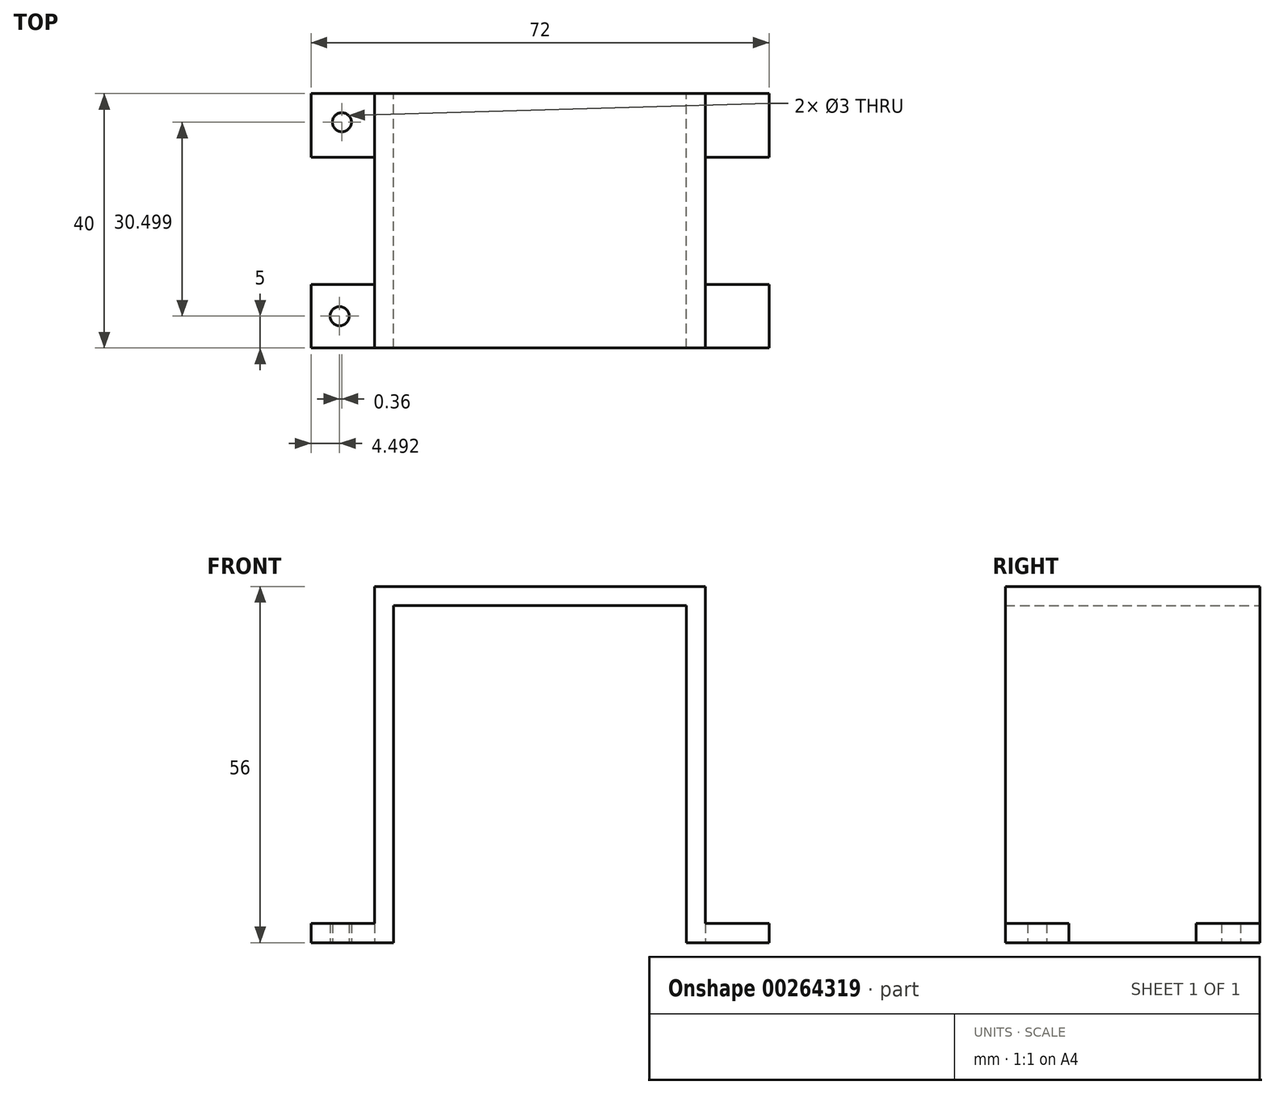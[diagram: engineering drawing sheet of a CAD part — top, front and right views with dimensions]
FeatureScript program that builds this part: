
annotation { "Feature Type Name" : "Feature", "Feature Type Description" : "" }
export const myFeature = defineFeature(function(context is Context, id is Id, definition is map)
    precondition{}
    {
        {
            var Q0;
            Q0=qCreatedBy(makeId("Front.planeOp"),FACE);
            var sketch = newSketch(context, id + "F0", { "sketchPlane" : qUnion([Q0])});
            skLineSegment(sketch, "E0", {"start": v(-56.16, -56) * mm, "end": v(-56.16, 0) * mm});
            skLineSegment(sketch, "E1", {"start": v(-56.16, 0) * mm, "end": v(-4.16, 0) * mm});
            skLineSegment(sketch, "E2", {"start": v(-4.16, 0) * mm, "end": v(-4.16, -56) * mm});
            skLineSegment(sketch, "E3", {"start": v(-4.16, -56) * mm, "end": v(-7.16, -56) * mm});
            skLineSegment(sketch, "E4", {"start": v(-7.16, -56) * mm, "end": v(-7.16, -3) * mm});
            skLineSegment(sketch, "E5", {"start": v(-7.16, -3) * mm, "end": v(-53.16, -3) * mm});
            skLineSegment(sketch, "E6", {"start": v(-56.16, -56) * mm, "end": v(-53.16, -56) * mm});
            skLineSegment(sketch, "E7", {"start": v(-53.16, -56) * mm, "end": v(-53.16, -3) * mm});
            skSolve(sketch);
        }
        {
            var Q0;
            Q0=makeQuery(id+"F0.imprint","IMPRINT",FACE,{"disambiguationData":[TD([[makeQuery(id+"F0.imprint","IMPRINT",EDGE,{"derivedFrom":sQuery(id+"F0.wireOp",EDGE,"trVvDC30-jFMu-2vVs-1iuF-PGvGUxvKBNX2.bottom")}),-1.0]])]});
            var Q1;
            Q1=makeQuery(id+"F0.imprint","IMPRINT",FACE,{"disambiguationData":[TD([[makeQuery(id+"F0.imprint","IMPRINT",EDGE,{"derivedFrom":sQuery(id+"F0.wireOp",EDGE,"E0")}),-1.0]])]});
            extrude(context, id + "F1", {"entities" : qUnion([Q0, Q1]), "depth" : 40 * mm});
        }
        {
            var Q0;
            Q0=makeQuery(id+"F1.opExtrude","SWEPT_FACE",FACE,{"disambiguationData":[OSD([sQuery(id+"F0.wireOp",EDGE,"E6")])]});
            var sketch = newSketch(context, id + "F2", { "sketchPlane" : qUnion([Q0])});
            skLineSegment(sketch, "E8.bottom", {"start": v(-56.16, 0) * mm, "end": v(-66.16, 0) * mm});
            skLineSegment(sketch, "E8.top", {"start": v(-56.16, 10) * mm, "end": v(-66.16, 10) * mm});
            skLineSegment(sketch, "E8.left", {"start": v(-56.16, 0) * mm, "end": v(-56.16, 10) * mm});
            skLineSegment(sketch, "E8.right", {"start": v(-66.16, 0) * mm, "end": v(-66.16, 10) * mm});
            skLineSegment(sketch, "E9.bottom", {"start": v(-56.16, 40) * mm, "end": v(-66.16, 40) * mm});
            skLineSegment(sketch, "E9.top", {"start": v(-56.16, 30) * mm, "end": v(-66.16, 30) * mm});
            skLineSegment(sketch, "E9.left", {"start": v(-56.16, 40) * mm, "end": v(-56.16, 30) * mm});
            skLineSegment(sketch, "E9.right", {"start": v(-66.16, 40) * mm, "end": v(-66.16, 30) * mm});
            skSolve(sketch);
        }
        {
            var Q0;
            Q0=makeQuery(id+"F1.opExtrude","SWEPT_FACE",FACE,{"disambiguationData":[OSD([sQuery(id+"F0.wireOp",EDGE,"E3")])]});
            var sketch = newSketch(context, id + "F3", { "sketchPlane" : qUnion([Q0])});
            skLineSegment(sketch, "E10.bottom", {"start": v(-4.16, 40) * mm, "end": v(5.84, 40) * mm});
            skLineSegment(sketch, "E10.top", {"start": v(-4.16, 30) * mm, "end": v(5.84, 30) * mm});
            skLineSegment(sketch, "E10.left", {"start": v(-4.16, 40) * mm, "end": v(-4.16, 30) * mm});
            skLineSegment(sketch, "E10.right", {"start": v(5.84, 40) * mm, "end": v(5.84, 30) * mm});
            skLineSegment(sketch, "E11.bottom", {"start": v(-4.16, 0) * mm, "end": v(5.84, 0) * mm});
            skLineSegment(sketch, "E11.top", {"start": v(-4.16, 10) * mm, "end": v(5.84, 10) * mm});
            skLineSegment(sketch, "E11.left", {"start": v(-4.16, 0) * mm, "end": v(-4.16, 10) * mm});
            skLineSegment(sketch, "E11.right", {"start": v(5.84, 0) * mm, "end": v(5.84, 10) * mm});
            skCircle(sketch, "E12", {"center": v(19.06, 35.17) * mm, "radius": 1.67 * mm});
            skSolve(sketch);
        }
        {
            var Q0;
            Q0=makeQuery(id+"F3.imprint","IMPRINT",FACE,{"disambiguationData":[TD([[makeQuery(id+"F3.imprint","IMPRINT",EDGE,{"derivedFrom":sQuery(id+"F3.wireOp",EDGE,"E11.bottom")}),1.0]])]});
            extrude(context, id + "F4", {"entities" : qUnion([Q0]), "operationType" : NewBodyOperationType.ADD, "oppositeDirection" : true, "depth" : 3 * mm});
        }
        {
            var Q0;
            Q0=makeQuery(id+"F2.imprint","IMPRINT",FACE,{"disambiguationData":[TD([[makeQuery(id+"F2.imprint","IMPRINT",EDGE,{"derivedFrom":sQuery(id+"F2.wireOp",EDGE,"E8.bottom")}),-1.0]])]});
            extrude(context, id + "F5", {"entities" : qUnion([Q0]), "operationType" : NewBodyOperationType.ADD, "oppositeDirection" : true, "depth" : 3 * mm});
        }
        {
            var Q0;
            Q0=makeQuery(id+"F4.boolean.opBoolean","MERGE",FACE,{"derivedFrom":[makeQuery(id+"F1.opExtrude","SWEPT_FACE",FACE,{"disambiguationData":[OSD([sQuery(id+"F0.wireOp",EDGE,"E3")])]}),makeQuery(id+"F4.opExtrude","CAP_FACE",FACE,{"disambiguationData":[OSD([sQuery(id+"F3.wireOp",EDGE,"E11.bottom"),sQuery(id+"F3.wireOp",EDGE,"E11.top"),sQuery(id+"F3.wireOp",EDGE,"E11.left"),sQuery(id+"F3.wireOp",EDGE,"E11.right")])],"isStart":true})]});
            var sketch = newSketch(context, id + "F6", { "sketchPlane" : qUnion([Q0])});
            skLineSegment(sketch, "E13.bottom", {"start": v(-4.16, 40) * mm, "end": v(5.84, 40) * mm});
            skLineSegment(sketch, "E13.top", {"start": v(-4.16, 30) * mm, "end": v(5.84, 30) * mm});
            skLineSegment(sketch, "E13.left", {"start": v(-4.16, 40) * mm, "end": v(-4.16, 30) * mm});
            skLineSegment(sketch, "E13.right", {"start": v(5.84, 40) * mm, "end": v(5.84, 30) * mm});
            skSolve(sketch);
        }
        {
            var Q0;
            Q0=makeQuery(id+"F6.imprint","IMPRINT",FACE,{"disambiguationData":[TD([[makeQuery(id+"F6.imprint","IMPRINT",EDGE,{"derivedFrom":sQuery(id+"F6.wireOp",EDGE,"E13.bottom")}),-1.0]])]});
            extrude(context, id + "F7", {"entities" : qUnion([Q0]), "operationType" : NewBodyOperationType.ADD, "oppositeDirection" : true, "depth" : 3 * mm});
        }
        {
            var Q0;
            Q0=makeQuery(id+"F5.boolean.opBoolean","MERGE",FACE,{"derivedFrom":[makeQuery(id+"F1.opExtrude","SWEPT_FACE",FACE,{"disambiguationData":[OSD([sQuery(id+"F0.wireOp",EDGE,"E6")])]}),makeQuery(id+"F5.opExtrude","CAP_FACE",FACE,{"disambiguationData":[OSD([sQuery(id+"F2.wireOp",EDGE,"E8.bottom"),sQuery(id+"F2.wireOp",EDGE,"E8.top"),sQuery(id+"F2.wireOp",EDGE,"E8.left"),sQuery(id+"F2.wireOp",EDGE,"E8.right")])],"isStart":true})]});
            var sketch = newSketch(context, id + "F8", { "sketchPlane" : qUnion([Q0])});
            skLineSegment(sketch, "E14.bottom", {"start": v(-56.16, 40) * mm, "end": v(-66.16, 40) * mm});
            skLineSegment(sketch, "E14.top", {"start": v(-56.16, 30) * mm, "end": v(-66.16, 30) * mm});
            skLineSegment(sketch, "E14.left", {"start": v(-56.16, 40) * mm, "end": v(-56.16, 30) * mm});
            skLineSegment(sketch, "E14.right", {"start": v(-66.16, 40) * mm, "end": v(-66.16, 30) * mm});
            skSolve(sketch);
        }
        {
            var Q0;
            Q0=makeQuery(id+"F8.imprint","IMPRINT",FACE,{"disambiguationData":[TD([[makeQuery(id+"F8.imprint","IMPRINT",EDGE,{"derivedFrom":sQuery(id+"F8.wireOp",EDGE,"E14.bottom")}),1.0]])]});
            extrude(context, id + "F9", {"entities" : qUnion([Q0]), "operationType" : NewBodyOperationType.ADD, "oppositeDirection" : true, "depth" : 3 * mm});
        }
        {
            var Q0;
            Q0=makeQuery(id+"F9.boolean.opBoolean","MERGE",FACE,{"derivedFrom":[makeQuery(id+"F5.boolean.opBoolean","MERGE",FACE,{"derivedFrom":[makeQuery(id+"F1.opExtrude","SWEPT_FACE",FACE,{"disambiguationData":[OSD([sQuery(id+"F0.wireOp",EDGE,"E6")])]}),makeQuery(id+"F5.opExtrude","CAP_FACE",FACE,{"disambiguationData":[OSD([sQuery(id+"F2.wireOp",EDGE,"E8.bottom"),sQuery(id+"F2.wireOp",EDGE,"E8.top"),sQuery(id+"F2.wireOp",EDGE,"E8.left"),sQuery(id+"F2.wireOp",EDGE,"E8.right")])],"isStart":true})]}),makeQuery(id+"F9.opExtrude","CAP_FACE",FACE,{"disambiguationData":[OSD([sQuery(id+"F8.wireOp",EDGE,"E14.bottom"),sQuery(id+"F8.wireOp",EDGE,"E14.top"),sQuery(id+"F8.wireOp",EDGE,"E14.left"),sQuery(id+"F8.wireOp",EDGE,"E14.right")])],"isStart":true})]});
            var sketch = newSketch(context, id + "F10", { "sketchPlane" : qUnion([Q0])});
            skCircle(sketch, "E15", {"center": v(-61.67, 35) * mm, "radius": 2.72 * mm});
            skPoint(sketch, "E15.centerSnap0", {"position": v(-66.16, 35) * mm});
            skCircle(sketch, "E16", {"center": v(-61.3, 4.5) * mm, "radius": 3 * mm});
            skCircle(sketch, "E17", {"center": v(19.4, 4.69) * mm, "radius": 3.62 * mm});
            skCircle(sketch, "E18", {"center": v(18.84, 95.13) * mm, "radius": 2.8 * mm});
            skSolve(sketch);
        }
        {
            var Q0;
            Q0=sQuery(id+"F10.wireOp",VERTEX,"E15.center");
            var Q1;
            Q1=sQuery(id+"F10.wireOp",VERTEX,"E18.center");
            var Q2;
            Q2=sQuery(id+"F10.wireOp",VERTEX,"E16.center");
            var Q3;
            Q3=sQuery(id+"F10.wireOp",VERTEX,"E17.center");
            var Q4;
            Q4=makeQuery(id+"F1.opExtrude","SWEPT_BODY",BODY,{"disambiguationData":[OSD([sQuery(id+"F0.wireOp",EDGE,"E0"),sQuery(id+"F0.wireOp",EDGE,"E1"),sQuery(id+"F0.wireOp",EDGE,"E2"),sQuery(id+"F0.wireOp",EDGE,"E3"),sQuery(id+"F0.wireOp",EDGE,"E4"),sQuery(id+"F0.wireOp",EDGE,"E5"),sQuery(id+"F0.wireOp",EDGE,"E6"),sQuery(id+"F0.wireOp",EDGE,"E7")])]});
            hole(context, id + "F11", {"style" : HoleStyle.SIMPLE, "endStyle" : HoleEndStyle.THROUGH, "holeDiameter" : 3 * mm, "tappedDepth" : 12 * mm, "tapClearance" : 3, "locations" : qUnion([Q0, Q1, Q2, Q3]), "scope" : qUnion([Q4])});
        }
        {
            var Q0;
            Q0=makeQuery(id+"F7.opExtrude","CAP_FACE",FACE,{"disambiguationData":[OSD([sQuery(id+"F6.wireOp",EDGE,"E13.bottom"),sQuery(id+"F6.wireOp",EDGE,"E13.top"),sQuery(id+"F6.wireOp",EDGE,"E13.left"),sQuery(id+"F6.wireOp",EDGE,"E13.right")])],"isStart":false});
            var sketch = newSketch(context, id + "F12", { "sketchPlane" : qUnion([Q0])});
            skCircle(sketch, "E19", {"center": v(18.9, -35.15) * mm, "radius": 1.5 * mm});
            skSolve(sketch);
        }
        {
            var Q0;
            Q0=sQuery(id+"F12.wireOp",VERTEX,"E19.center");
            var Q1;
            Q1=makeQuery(id+"F1.opExtrude","SWEPT_BODY",BODY,{"disambiguationData":[OSD([sQuery(id+"F0.wireOp",EDGE,"E0"),sQuery(id+"F0.wireOp",EDGE,"E1"),sQuery(id+"F0.wireOp",EDGE,"E2"),sQuery(id+"F0.wireOp",EDGE,"E3"),sQuery(id+"F0.wireOp",EDGE,"E4"),sQuery(id+"F0.wireOp",EDGE,"E5"),sQuery(id+"F0.wireOp",EDGE,"E6"),sQuery(id+"F0.wireOp",EDGE,"E7")])]});
            hole(context, id + "F13", {"style" : HoleStyle.SIMPLE, "endStyle" : HoleEndStyle.THROUGH, "holeDiameter" : 3 * mm, "tappedDepth" : 12 * mm, "tapClearance" : 3, "locations" : qUnion([Q0]), "scope" : qUnion([Q1])});
        }
    });
